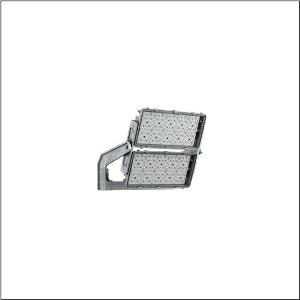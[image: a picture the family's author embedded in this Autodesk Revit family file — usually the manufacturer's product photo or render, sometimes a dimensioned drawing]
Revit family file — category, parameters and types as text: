
# Revit family: floodlight_fl_11_maxi_remote___rs07_5xa779514k01ba_6340
name_source: partatom
category: Lighting Fixtures
units: mm (PartAtom-declared; Revit-internal decimal feet)

## family parameters
Cut with Voids When Loaded = No
Host = Face
Light Source = No
Part Type = Normal
Room Calculation Point = No
Round Connector Dimension = Use Diameter
Shared = No

## types (1)
- --- (1 x LED, 75300 lm, 707.9 W, 5700K)
    Apparent Load = 708 VA
    CIE Flux Codes = 80 93 99 100 99
    Color Rendering = 90
    Color Temperature = 5700K
    Default Elevation = 1800 mm
    Description = Floodlight FL 11  maxi  Remote floodlight; light control with lens of PMMA; cover panel of toughened safety glass, transparent; light distribution: RS07, rotationally symmetric direct distribution, LEDcolour temperature: 5700K, rated luminous flux: 75.300lm, colour rendering: CRI > 90, light colour: 957; luminous efficacy: 106lm/W; brightness control: DMX+RDM; with terminal, 8-pole, max. 2.5mm², mains connection: 220..240V/380..400V AC, 50/60Hz, surge voltage resistance: line to ground: 10kV, ECG replaceable separately, LED unit replaceable without ESD environment, dustproof LED module, dimming range 10..100%; 708W floodlight with 2x LED unit of diecast aluminium, coated grey; length: 713mm / width: 651mm / height: 338mm; mounting bracket, of diecast aluminium, uncoated, natural, equipment: Longlife, protection rating (complete): IP66; insulation class (complete): insulation class I (protective earthing); certification: CE, ENEC, VDE; ball protection: ball impact resistance with accessories, impact resistance: IK07; only for outdoor installations, rated ambient temperature 10°C, permissible operating ambient temperature: -40..+40°C, permissible storage temperature: -40..+85°C; packaging unit: 1 piece

Light Distribution: RS07
    Height = 320 mm
    Lamp = 1 x LED
    Lamp Light Flux = 75300 lm
    Lamp Power = 707.9 W
    Lamp count = 1
    Length = 712 mm
    Luminous efficacy = 106 lm/W
    Manufacturer = Siteco
    ModVariant = No
    Model = 5XA779514K01BA
    Mounting Place = Ceiling
    Mounting Type = Surface mounted
    Number of Poles = 1
    OnlyDefault = Yes
    Power Factor = 1
    Product Name = Floodlight FL 11 maxi Remote | RS07
    Product group = floodlight | ceiling mounted
    ProductGroupID = 302
    Protection Class = Protection class I
    Protection Degree = IP 66
    RLX_Detail_Level = 1
    RLX_Emergency_Light_Flux = 0 lm
    RLX_Emergency_Type = 0
    RLX_Emergency_Type_DB = No
    RlxData = <blob elided: 41185 chars, md5=242a3b0b>
    Socket = socket
    Standby Power = 0 W
    System Light Flux = 75300 lm
    System Power = 708 W
    Type Comments = factory setting: luminous flux: 100 % | dim-lin: 254 | 740 mA
    Type Image = l_1006788.jpg
    URL = http://relux.com
    VarID = @adj_152953
    Voltage = 0 V
    Weight = 0.00 kg
    Width = 655 mm

## geometry (parser evidence)
native form markers: Blend x4, Sweep x13
no freeform markers — native parametric forms only
